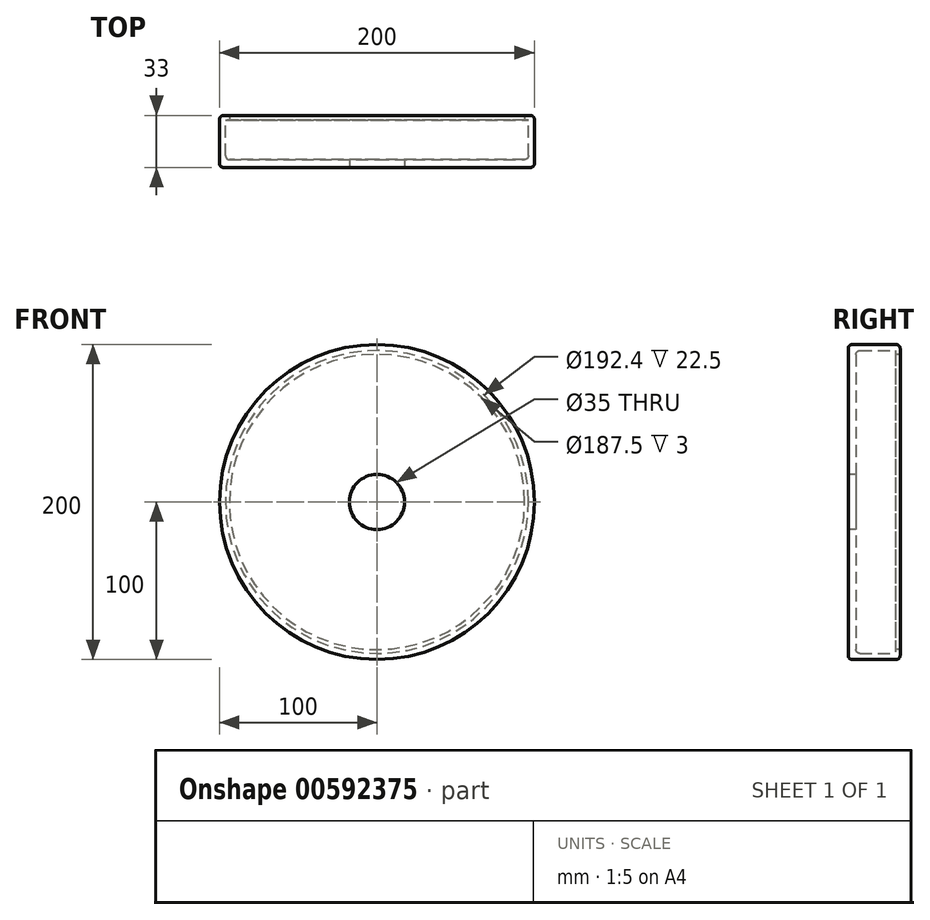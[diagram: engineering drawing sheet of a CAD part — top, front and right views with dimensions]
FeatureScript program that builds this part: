
annotation { "Feature Type Name" : "Feature", "Feature Type Description" : "" }
export const myFeature = defineFeature(function(context is Context, id is Id, definition is map)
    precondition{}
    {
        {
            var Q0;
            Q0=qCreatedBy(makeId("Front.planeOp"),FACE);
            var sketch = newSketch(context, id + "F0", { "sketchPlane" : qUnion([Q0])});
            skCircle(sketch, "E0", {"center": v(0, 0) * mm, "radius": 100 * mm});
            skSolve(sketch);
        }
        {
            var Q0;
            Q0 = qSketchRegion(id + "F0", true);
            extrude(context, id + "F1", {"entities" : qUnion([Q0]), "depth" : 15 * mm, "offsetDistance" : 25 * mm, "hasSecondDirection" : true, "secondDirectionOppositeDirection" : true, "secondDirectionDepth" : 15 * mm});
        }
        {
            var Q0;
            Q0=makeQuery(id+"F1.opExtrude","CAP_FACE",FACE,{"disambiguationData":[OSD([sQuery(id+"F0.wireOp",EDGE,"E0")])],"isStart":true});
            var sketch = newSketch(context, id + "F2", { "sketchPlane" : qUnion([Q0])});
            skCircle(sketch, "E1", {"center": v(0, 0) * mm, "radius": 96.2 * mm});
            skSolve(sketch);
        }
        {
            var Q0;
            Q0 = qSketchRegion(id + "F2", true);
            extrude(context, id + "F3", {"entities" : qUnion([Q0]), "operationType" : NewBodyOperationType.REMOVE, "oppositeDirection" : true, "depth" : 25 * mm, "offsetDistance" : 25 * mm});
        }
        {
            var Q0;
            Q0=makeQuery(id+"F3.boolean.opBoolean","COPY",EDGE,{"derivedFrom":makeQuery(id+"F3.opExtrude","CAP_EDGE",EDGE,{"disambiguationData":[OSD([sQuery(id+"F2.wireOp",EDGE,"E1")])],"isStart":false})});
            fillet(context, id + "F4", {"entities" : qUnion([Q0]), "radius" : 2.5 * mm, "tangentPropagation" : true, "allowEdgeOverflow" : false});
        }
        {
            var Q0;
            Q0=makeQuery(id+"F1.opExtrude","CAP_EDGE",EDGE,{"disambiguationData":[OSD([sQuery(id+"F0.wireOp",EDGE,"E0")])],"isStart":false});
            fillet(context, id + "F5", {"entities" : qUnion([Q0]), "radius" : 2.5 * mm, "tangentPropagation" : true, "allowEdgeOverflow" : false});
        }
        {
            var Q0;
            Q0=makeQuery(id+"F1.opExtrude","CAP_FACE",FACE,{"disambiguationData":[OSD([sQuery(id+"F0.wireOp",EDGE,"E0")])],"isStart":false});
            var sketch = newSketch(context, id + "F6", { "sketchPlane" : qUnion([Q0])});
            skCircle(sketch, "E2", {"center": v(0, 0) * mm, "radius": 17.5 * mm});
            skSolve(sketch);
        }
        {
            var Q0;
            Q0 = qSketchRegion(id + "F6", true);
            extrude(context, id + "F7", {"entities" : qUnion([Q0]), "operationType" : NewBodyOperationType.REMOVE, "endBound" : BoundingType.THROUGH_ALL, "oppositeDirection" : true, "depth" : 25 * mm, "offsetDistance" : 25 * mm});
        }
        {
            var Q0;
            Q0=makeQuery(id+"F1.opExtrude","CAP_FACE",FACE,{"disambiguationData":[OSD([sQuery(id+"F0.wireOp",EDGE,"E0")])],"isStart":true});
            var sketch = newSketch(context, id + "F8", { "sketchPlane" : qUnion([Q0])});
            skCircle(sketch, "E3", {"center": v(0, 0) * mm, "radius": 100 * mm});
            skCircle(sketch, "E4", {"center": v(0, 0) * mm, "radius": 93.75 * mm});
            skSolve(sketch);
        }
        {
            var Q0;
            Q0 = qSketchRegion(id + "F8", true);
            extrude(context, id + "F9", {"entities" : qUnion([Q0]), "operationType" : NewBodyOperationType.ADD, "depth" : 3 * mm, "offsetDistance" : 25 * mm});
        }
        {
            var Q0;
            Q0=makeQuery(id+"F9.opExtrude","CAP_EDGE",EDGE,{"disambiguationData":[OSD([sQuery(id+"F8.wireOp",EDGE,"E3")])],"isStart":false});
            fillet(context, id + "F10", {"entities" : qUnion([Q0]), "radius" : 2.5 * mm, "tangentPropagation" : true, "allowEdgeOverflow" : false});
        }
    });
